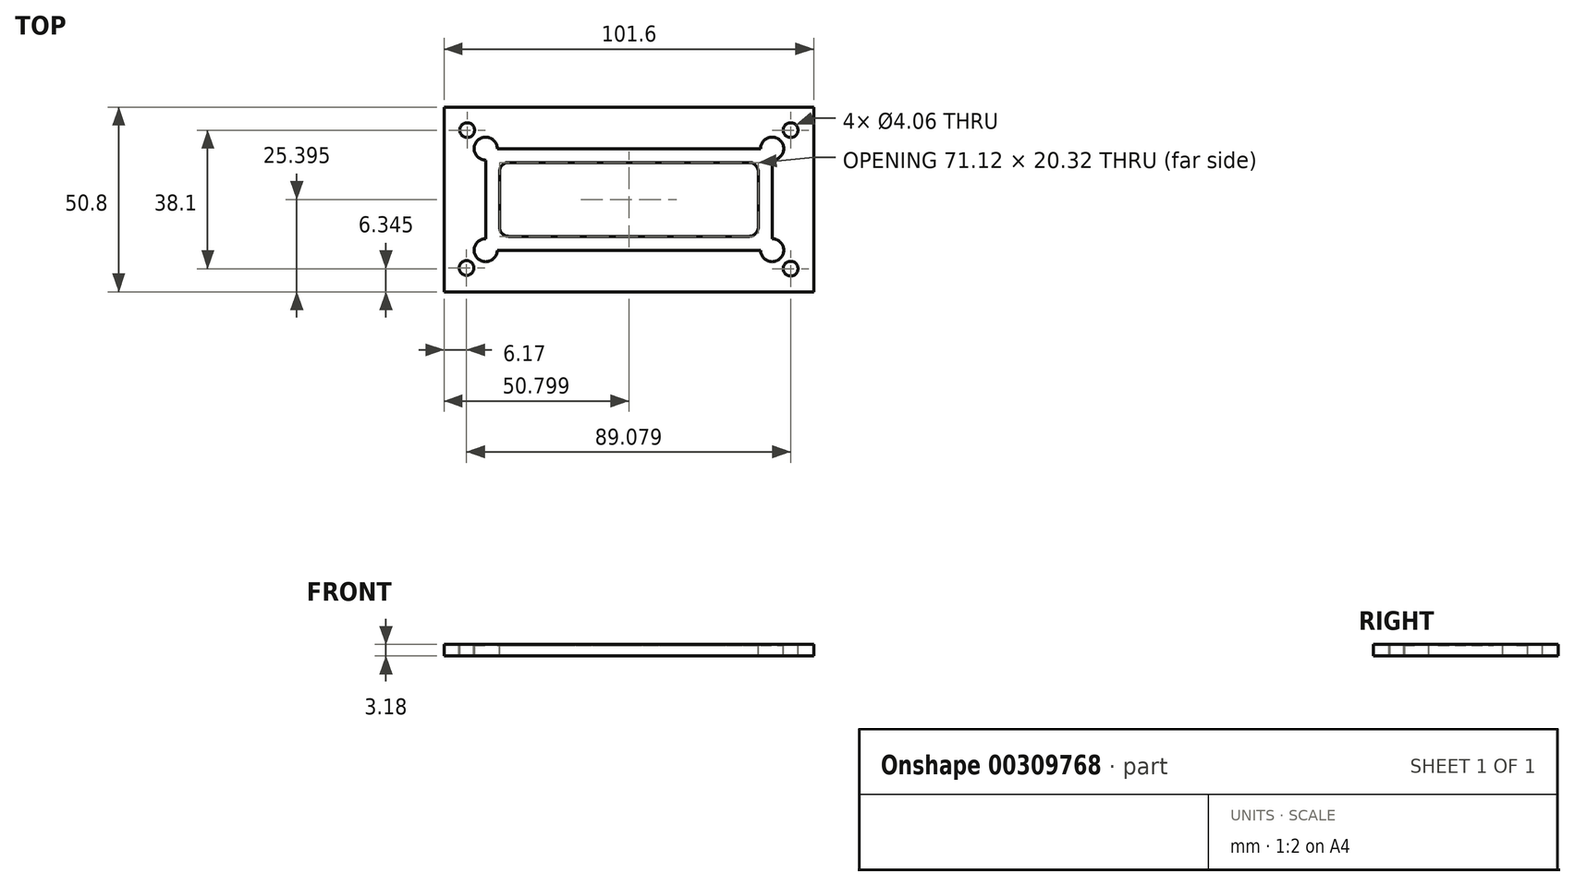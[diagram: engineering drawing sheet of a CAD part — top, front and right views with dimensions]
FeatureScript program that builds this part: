
annotation { "Feature Type Name" : "Feature", "Feature Type Description" : "" }
export const myFeature = defineFeature(function(context is Context, id is Id, definition is map)
    precondition{}
    {
        {
            var Q0;
            Q0=qCreatedBy(makeId("Top.planeOp"),FACE);
            var sketch = newSketch(context, id + "F0", { "sketchPlane" : qUnion([Q0])});
            skLineSegment(sketch, "E0.bottom", {"start": v(0.18, 50.6) * mm, "end": v(101.78, 50.6) * mm});
            skLineSegment(sketch, "E0.top", {"start": v(0.18, -0.2) * mm, "end": v(101.78, -0.2) * mm});
            skLineSegment(sketch, "E0.left", {"start": v(0.18, 50.6) * mm, "end": v(0.18, -0.2) * mm});
            skLineSegment(sketch, "E0.right", {"start": v(101.78, 50.6) * mm, "end": v(101.78, -0.2) * mm});
            skSolve(sketch);
        }
        {
            var Q0;
            Q0=makeQuery(id+"F0.imprint","IMPRINT",FACE,{"disambiguationData":[TD([[makeQuery(id+"F0.imprint","IMPRINT",EDGE,{"derivedFrom":sQuery(id+"F0.wireOp",EDGE,"E0.bottom")}),-1.0]])]});
            extrude(context, id + "F1", {"entities" : qUnion([Q0]), "depth" : 3.17 * mm});
        }
        {
            var Q0;
            Q0=makeQuery(id+"F1.opExtrude","CAP_FACE",FACE,{"disambiguationData":[OSD([sQuery(id+"F0.wireOp",EDGE,"E0.bottom"),sQuery(id+"F0.wireOp",EDGE,"E0.top"),sQuery(id+"F0.wireOp",EDGE,"E0.left"),sQuery(id+"F0.wireOp",EDGE,"E0.right")])],"isStart":false});
            var sketch = newSketch(context, id + "F2", { "sketchPlane" : qUnion([Q0])});
            skLineSegment(sketch, "E1.bottom", {"start": v(11.6, 39.17) * mm, "end": v(90.35, 39.17) * mm});
            skLineSegment(sketch, "E1.top", {"start": v(11.6, 11.23) * mm, "end": v(90.35, 11.23) * mm});
            skLineSegment(sketch, "E1.left", {"start": v(11.6, 39.17) * mm, "end": v(11.6, 11.23) * mm});
            skLineSegment(sketch, "E1.right", {"start": v(90.35, 39.17) * mm, "end": v(90.35, 11.23) * mm});
            skCircle(sketch, "E2", {"center": v(11.6, 39.17) * mm, "radius": 3.18 * mm});
            skCircle(sketch, "E3", {"center": v(11.6, 11.23) * mm, "radius": 3.18 * mm});
            skCircle(sketch, "E4", {"center": v(90.35, 39.17) * mm, "radius": 3.18 * mm});
            skCircle(sketch, "E5", {"center": v(90.35, 11.23) * mm, "radius": 3.18 * mm});
            skSolve(sketch);
        }
        {
            var Q0;
            {var subQ0=sQuery(id+"F2.wireOp",EDGE,"E1.left");var subQ1=sQuery(id+"F2.wireOp",EDGE,"E1.bottom");var subQ2=makeQuery(id+"F2.imprint","INTERSECT",VERTEX,{"derivedFrom":[subQ1,subQ0]});Q0=makeQuery(id+"F2.imprint","IMPRINT",FACE,{"disambiguationData":[TD([[makeQuery(id+"F2.imprint","IMPRINT",EDGE,{"disambiguationData":[TD([[subQ2,-1.0]])],"derivedFrom":subQ1}),1.0]])]});}
            var Q1;
            {var subQ0=sQuery(id+"F2.wireOp",EDGE,"E1.left");var subQ1=sQuery(id+"F2.wireOp",EDGE,"E1.bottom");var subQ2=makeQuery(id+"F2.imprint","INTERSECT",VERTEX,{"derivedFrom":[subQ1,subQ0]});Q1=makeQuery(id+"F2.imprint","IMPRINT",FACE,{"disambiguationData":[TD([[makeQuery(id+"F2.imprint","IMPRINT",EDGE,{"disambiguationData":[TD([[subQ2,-1.0]])],"derivedFrom":subQ1}),-1.0]])]});}
            var Q2;
            {var subQ0=sQuery(id+"F2.wireOp",EDGE,"E1.left");var subQ1=sQuery(id+"F2.wireOp",EDGE,"E1.top");var subQ2=makeQuery(id+"F2.imprint","INTERSECT",VERTEX,{"derivedFrom":[subQ1,subQ0]});Q2=makeQuery(id+"F2.imprint","IMPRINT",FACE,{"disambiguationData":[TD([[makeQuery(id+"F2.imprint","IMPRINT",EDGE,{"disambiguationData":[TD([[subQ2,-1.0]])],"derivedFrom":subQ1}),1.0]])]});}
            var Q3;
            {var subQ0=sQuery(id+"F2.wireOp",EDGE,"E1.left");var subQ1=sQuery(id+"F2.wireOp",EDGE,"E1.top");var subQ2=makeQuery(id+"F2.imprint","INTERSECT",VERTEX,{"derivedFrom":[subQ1,subQ0]});Q3=makeQuery(id+"F2.imprint","IMPRINT",FACE,{"disambiguationData":[TD([[makeQuery(id+"F2.imprint","IMPRINT",EDGE,{"disambiguationData":[TD([[subQ2,-1.0]])],"derivedFrom":subQ1}),-1.0]])]});}
            var Q4;
            {var subQ0=sQuery(id+"F2.wireOp",EDGE,"E1.right");var subQ1=sQuery(id+"F2.wireOp",EDGE,"E1.top");var subQ2=makeQuery(id+"F2.imprint","INTERSECT",VERTEX,{"derivedFrom":[subQ1,subQ0]});Q4=makeQuery(id+"F2.imprint","IMPRINT",FACE,{"disambiguationData":[TD([[makeQuery(id+"F2.imprint","IMPRINT",EDGE,{"disambiguationData":[TD([[subQ2,1.0]])],"derivedFrom":subQ1}),1.0]])]});}
            var Q5;
            {var subQ0=sQuery(id+"F2.wireOp",EDGE,"E1.right");var subQ1=sQuery(id+"F2.wireOp",EDGE,"E1.top");var subQ2=makeQuery(id+"F2.imprint","INTERSECT",VERTEX,{"derivedFrom":[subQ1,subQ0]});Q5=makeQuery(id+"F2.imprint","IMPRINT",FACE,{"disambiguationData":[TD([[makeQuery(id+"F2.imprint","IMPRINT",EDGE,{"disambiguationData":[TD([[subQ2,1.0]])],"derivedFrom":subQ1}),-1.0]])]});}
            var Q6;
            {var subQ0=sQuery(id+"F2.wireOp",EDGE,"E1.right");var subQ1=sQuery(id+"F2.wireOp",EDGE,"E1.bottom");var subQ2=makeQuery(id+"F2.imprint","INTERSECT",VERTEX,{"derivedFrom":[subQ1,subQ0]});Q6=makeQuery(id+"F2.imprint","IMPRINT",FACE,{"disambiguationData":[TD([[makeQuery(id+"F2.imprint","IMPRINT",EDGE,{"disambiguationData":[TD([[subQ2,1.0]])],"derivedFrom":subQ1}),1.0]])]});}
            var Q7;
            {var subQ0=sQuery(id+"F2.wireOp",EDGE,"E1.right");var subQ1=sQuery(id+"F2.wireOp",EDGE,"E1.bottom");var subQ2=makeQuery(id+"F2.imprint","INTERSECT",VERTEX,{"derivedFrom":[subQ1,subQ0]});Q7=makeQuery(id+"F2.imprint","IMPRINT",FACE,{"disambiguationData":[TD([[makeQuery(id+"F2.imprint","IMPRINT",EDGE,{"disambiguationData":[TD([[subQ2,1.0]])],"derivedFrom":subQ1}),-1.0]])]});}
            var Q8;
            {var subQ5=sQuery(id+"F2.wireOp",EDGE,"E2");var subQ13=sQuery(id+"F2.wireOp",EDGE,"E1.bottom");var subQ14=makeQuery(id+"F2.imprint","INTERSECT",VERTEX,{"derivedFrom":[subQ13,subQ5]});Q8=makeQuery(id+"F2.imprint","IMPRINT",FACE,{"disambiguationData":[TD([[makeQuery(id+"F2.imprint","IMPRINT",EDGE,{"disambiguationData":[TD([[subQ14,-1.0]])],"derivedFrom":subQ13}),-1.0]])]});}
            extrude(context, id + "F3", {"entities" : qUnion([Q0, Q1, Q2, Q3, Q4, Q5, Q6, Q7, Q8]), "operationType" : NewBodyOperationType.REMOVE, "oppositeDirection" : true, "depth" : 0.25 * mm});
        }
        {
            var Q0;
            Q0=makeQuery(id+"F3.boolean.opBoolean","COPY",FACE,{"derivedFrom":makeQuery(id+"F3.opExtrude","CAP_FACE",FACE,{"disambiguationData":[OSD([sQuery(id+"F2.wireOp",EDGE,"E1.bottom"),sQuery(id+"F2.wireOp",EDGE,"E1.top"),sQuery(id+"F2.wireOp",EDGE,"E1.left"),sQuery(id+"F2.wireOp",EDGE,"E1.right"),sQuery(id+"F2.wireOp",EDGE,"E2"),sQuery(id+"F2.wireOp",EDGE,"E3"),sQuery(id+"F2.wireOp",EDGE,"E4"),sQuery(id+"F2.wireOp",EDGE,"E5")])],"isStart":false})});
            var sketch = newSketch(context, id + "F4", { "sketchPlane" : qUnion([Q0])});
            skLineSegment(sketch, "E6.bottom", {"start": v(17.96, 15.04) * mm, "end": v(84, 15.04) * mm});
            skLineSegment(sketch, "E6.top", {"start": v(17.96, 35.36) * mm, "end": v(84, 35.36) * mm});
            skLineSegment(sketch, "E6.left", {"start": v(15.42, 17.58) * mm, "end": v(15.42, 32.82) * mm});
            skLineSegment(sketch, "E6.right", {"start": v(86.54, 17.58) * mm, "end": v(86.54, 32.82) * mm});
            skPoint(sketch, "E7.visualSharp", {"position": v(86.54, 35.36) * mm});
            skArc(sketch, "E7.filletArc", {"start": v(86.54, 32.82) * mm, "mid": v(85.8, 34.61) * mm, "end": v(84, 35.36) * mm});
            skPoint(sketch, "E8.visualSharp", {"position": v(86.54, 15.04) * mm});
            skArc(sketch, "E8.filletArc", {"start": v(84, 15.04) * mm, "mid": v(85.8, 15.78) * mm, "end": v(86.54, 17.58) * mm});
            skPoint(sketch, "E9.visualSharp", {"position": v(15.42, 15.04) * mm});
            skArc(sketch, "E9.filletArc", {"start": v(15.42, 17.58) * mm, "mid": v(16.16, 15.78) * mm, "end": v(17.96, 15.04) * mm});
            skPoint(sketch, "E10.visualSharp", {"position": v(15.42, 35.36) * mm});
            skArc(sketch, "E10.filletArc", {"start": v(17.96, 35.36) * mm, "mid": v(16.16, 34.61) * mm, "end": v(15.42, 32.82) * mm});
            skSolve(sketch);
        }
        {
            var Q0;
            Q0 = qSketchRegion(id + "F4", true);
            extrude(context, id + "F5", {"entities" : qUnion([Q0]), "operationType" : NewBodyOperationType.REMOVE, "oppositeDirection" : true, "depth" : 25.4 * mm, "hasSecondDirection" : true, "secondDirectionOppositeDirection" : false, "secondDirectionDepth" : 25.4 * mm});
        }
        {
            var Q0;
            Q0=makeQuery(id+"F1.opExtrude","CAP_FACE",FACE,{"disambiguationData":[OSD([sQuery(id+"F0.wireOp",EDGE,"E0.bottom"),sQuery(id+"F0.wireOp",EDGE,"E0.top"),sQuery(id+"F0.wireOp",EDGE,"E0.left"),sQuery(id+"F0.wireOp",EDGE,"E0.right")])],"isStart":false});
            var sketch = newSketch(context, id + "F6", { "sketchPlane" : qUnion([Q0])});
            skCircle(sketch, "E11", {"center": v(6.53, 44.25) * mm, "radius": 2.03 * mm});
            skCircle(sketch, "E12", {"center": v(95.43, 44.25) * mm, "radius": 2.03 * mm});
            skCircle(sketch, "E13", {"center": v(95.43, 6.15) * mm, "radius": 2.03 * mm});
            skCircle(sketch, "E14", {"center": v(6.35, 6.35) * mm, "radius": 2.03 * mm});
            skSolve(sketch);
        }
        {
            var Q0;
            Q0=makeQuery(id+"F6.imprint","IMPRINT",FACE,{"disambiguationData":[TD([[makeQuery(id+"F6.imprint","IMPRINT",EDGE,{"derivedFrom":sQuery(id+"F6.wireOp",EDGE,"E11")}),1.0]])]});
            var Q1;
            Q1=makeQuery(id+"F6.imprint","IMPRINT",FACE,{"disambiguationData":[TD([[makeQuery(id+"F6.imprint","IMPRINT",EDGE,{"derivedFrom":sQuery(id+"F6.wireOp",EDGE,"E12")}),1.0]])]});
            var Q2;
            Q2=makeQuery(id+"F6.imprint","IMPRINT",FACE,{"disambiguationData":[TD([[makeQuery(id+"F6.imprint","IMPRINT",EDGE,{"derivedFrom":sQuery(id+"F6.wireOp",EDGE,"E13")}),1.0]])]});
            var Q3;
            Q3=makeQuery(id+"F6.imprint","IMPRINT",FACE,{"disambiguationData":[TD([[makeQuery(id+"F6.imprint","IMPRINT",EDGE,{"derivedFrom":sQuery(id+"F6.wireOp",EDGE,"E14")}),1.0]])]});
            extrude(context, id + "F7", {"entities" : qUnion([Q0, Q1, Q2, Q3]), "operationType" : NewBodyOperationType.REMOVE, "oppositeDirection" : true, "depth" : 25.4 * mm, "hasSecondDirection" : true, "secondDirectionOppositeDirection" : false, "secondDirectionDepth" : 25.4 * mm});
        }
    });
